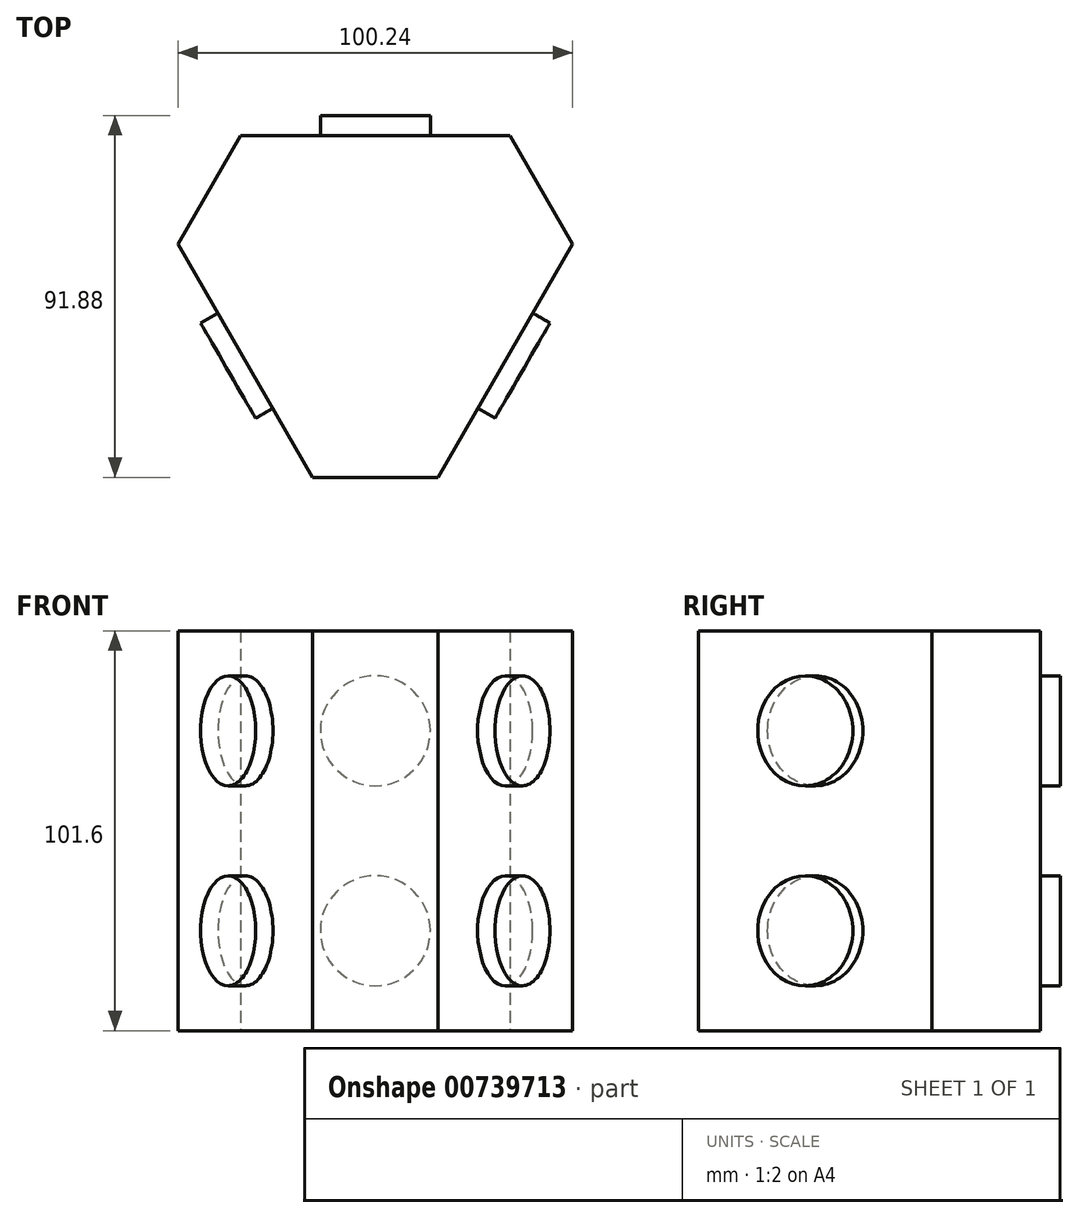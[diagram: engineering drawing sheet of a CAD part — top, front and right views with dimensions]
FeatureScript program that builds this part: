
annotation { "Feature Type Name" : "Feature", "Feature Type Description" : "" }
export const myFeature = defineFeature(function(context is Context, id is Id, definition is map)
    precondition{}
    {
        {
            var Q0;
            Q0=qCreatedBy(makeId("Top.planeOp"),FACE);
            var sketch = newSketch(context, id + "F0", { "sketchPlane" : qUnion([Q0])});
            skCircle(sketch, "E0.cCircle", {"center": v(0, 0) * mm, "radius": 76.2 * mm, "construction": true});
            skLineSegment(sketch, "E0.0", {"start": v(-15.87, -48.7) * mm, "end": v(-50.12, 10.6) * mm});
            skLineSegment(sketch, "E0.1", {"start": v(-34.24, 38.1) * mm, "end": v(34.24, 38.1) * mm});
            skLineSegment(sketch, "E0.2", {"start": v(50.12, 10.6) * mm, "end": v(15.88, -48.7) * mm});
            skLineSegment(sketch, "E1", {"start": v(-34.24, 38.1) * mm, "end": v(-50.12, 10.6) * mm});
            skLineSegment(sketch, "E2", {"start": v(-15.87, -48.7) * mm, "end": v(15.88, -48.7) * mm});
            skLineSegment(sketch, "E3", {"start": v(50.12, 10.6) * mm, "end": v(34.24, 38.1) * mm});
            skLineSegment(sketch, "E4", {"start": v(66, 38.1) * mm, "end": v(-33, -19.05) * mm, "construction": true});
            skLineSegment(sketch, "E5", {"start": v(0, -76.2) * mm, "end": v(0, 38.1) * mm, "construction": true});
            skLineSegment(sketch, "E6", {"start": v(-66, 38.1) * mm, "end": v(33, -19.05) * mm, "construction": true});
            skSolve(sketch);
        }
        {
            var Q0;
            Q0=makeQuery(id+"F0.imprint","IMPRINT",FACE,{"disambiguationData":[TD([[makeQuery(id+"F0.imprint","IMPRINT",EDGE,{"derivedFrom":sQuery(id+"F0.wireOp",EDGE,"E0.0")}),-1.0]])]});
            extrude(context, id + "F1", {"entities" : qUnion([Q0]), "depth" : 101.6 * mm, "offsetDistance" : 25.4 * mm});
        }
        {
            var Q0;
            Q0=makeQuery(id+"F1.opExtrude","SWEPT_FACE",FACE,{"disambiguationData":[OSD([sQuery(id+"F0.wireOp",EDGE,"E0.0")])]});
            var sketch = newSketch(context, id + "F2", { "sketchPlane" : qUnion([Q0])});
            skCircle(sketch, "E7", {"center": v(0, 76.2) * mm, "radius": 13.97 * mm});
            skCircle(sketch, "E8", {"center": v(0, 25.4) * mm, "radius": 13.97 * mm});
            skSolve(sketch);
        }
        {
            var Q0;
            Q0=makeQuery(id+"F2.imprint","IMPRINT",FACE,{"disambiguationData":[TD([[makeQuery(id+"F2.imprint","IMPRINT",EDGE,{"derivedFrom":sQuery(id+"F2.wireOp",EDGE,"E7")}),1.0]])]});
            var Q1;
            Q1=makeQuery(id+"F2.imprint","IMPRINT",FACE,{"disambiguationData":[TD([[makeQuery(id+"F2.imprint","IMPRINT",EDGE,{"derivedFrom":sQuery(id+"F2.wireOp",EDGE,"E8")}),1.0]])]});
            var Q2;
            Q2=sQuery(id+"F2.wireOp",EDGE,"E7");
            var Q3;
            Q3=sQuery(id+"F2.wireOp",EDGE,"E8");
            extrude(context, id + "F3", {"entities" : qUnion([Q0, Q1]), "operationType" : NewBodyOperationType.ADD, "surfaceEntities" : qUnion([Q2, Q3]), "depth" : 5.08 * mm, "offsetDistance" : 25.4 * mm});
        }
        {
            var Q0;
            Q0=makeQuery(id+"F1.opExtrude","SWEPT_FACE",FACE,{"disambiguationData":[OSD([sQuery(id+"F0.wireOp",EDGE,"E0.1")])]});
            var sketch = newSketch(context, id + "F4", { "sketchPlane" : qUnion([Q0])});
            skCircle(sketch, "E9", {"center": v(0, 76.2) * mm, "radius": 13.97 * mm});
            skCircle(sketch, "E10", {"center": v(0, 25.4) * mm, "radius": 13.97 * mm});
            skSolve(sketch);
        }
        {
            var Q0;
            Q0=makeQuery(id+"F4.imprint","IMPRINT",FACE,{"disambiguationData":[TD([[makeQuery(id+"F4.imprint","IMPRINT",EDGE,{"derivedFrom":sQuery(id+"F4.wireOp",EDGE,"E9")}),1.0]])]});
            var Q1;
            Q1=makeQuery(id+"F4.imprint","IMPRINT",FACE,{"disambiguationData":[TD([[makeQuery(id+"F4.imprint","IMPRINT",EDGE,{"derivedFrom":sQuery(id+"F4.wireOp",EDGE,"E10")}),1.0]])]});
            extrude(context, id + "F5", {"entities" : qUnion([Q0, Q1]), "operationType" : NewBodyOperationType.ADD, "depth" : 5.08 * mm, "offsetDistance" : 25.4 * mm});
        }
        {
            var Q0;
            Q0=makeQuery(id+"F1.opExtrude","SWEPT_FACE",FACE,{"disambiguationData":[OSD([sQuery(id+"F0.wireOp",EDGE,"E0.2")])]});
            var sketch = newSketch(context, id + "F6", { "sketchPlane" : qUnion([Q0])});
            skCircle(sketch, "E11", {"center": v(0, 76.2) * mm, "radius": 13.97 * mm});
            skCircle(sketch, "E12", {"center": v(0, 25.4) * mm, "radius": 13.97 * mm});
            skSolve(sketch);
        }
        {
            var Q0;
            Q0=makeQuery(id+"F6.imprint","IMPRINT",FACE,{"disambiguationData":[TD([[makeQuery(id+"F6.imprint","IMPRINT",EDGE,{"derivedFrom":sQuery(id+"F6.wireOp",EDGE,"E11")}),1.0]])]});
            var Q1;
            Q1=makeQuery(id+"F6.imprint","IMPRINT",FACE,{"disambiguationData":[TD([[makeQuery(id+"F6.imprint","IMPRINT",EDGE,{"derivedFrom":sQuery(id+"F6.wireOp",EDGE,"E12")}),1.0]])]});
            extrude(context, id + "F7", {"entities" : qUnion([Q0, Q1]), "operationType" : NewBodyOperationType.ADD, "depth" : 5.08 * mm, "offsetDistance" : 25.4 * mm});
        }
    });
